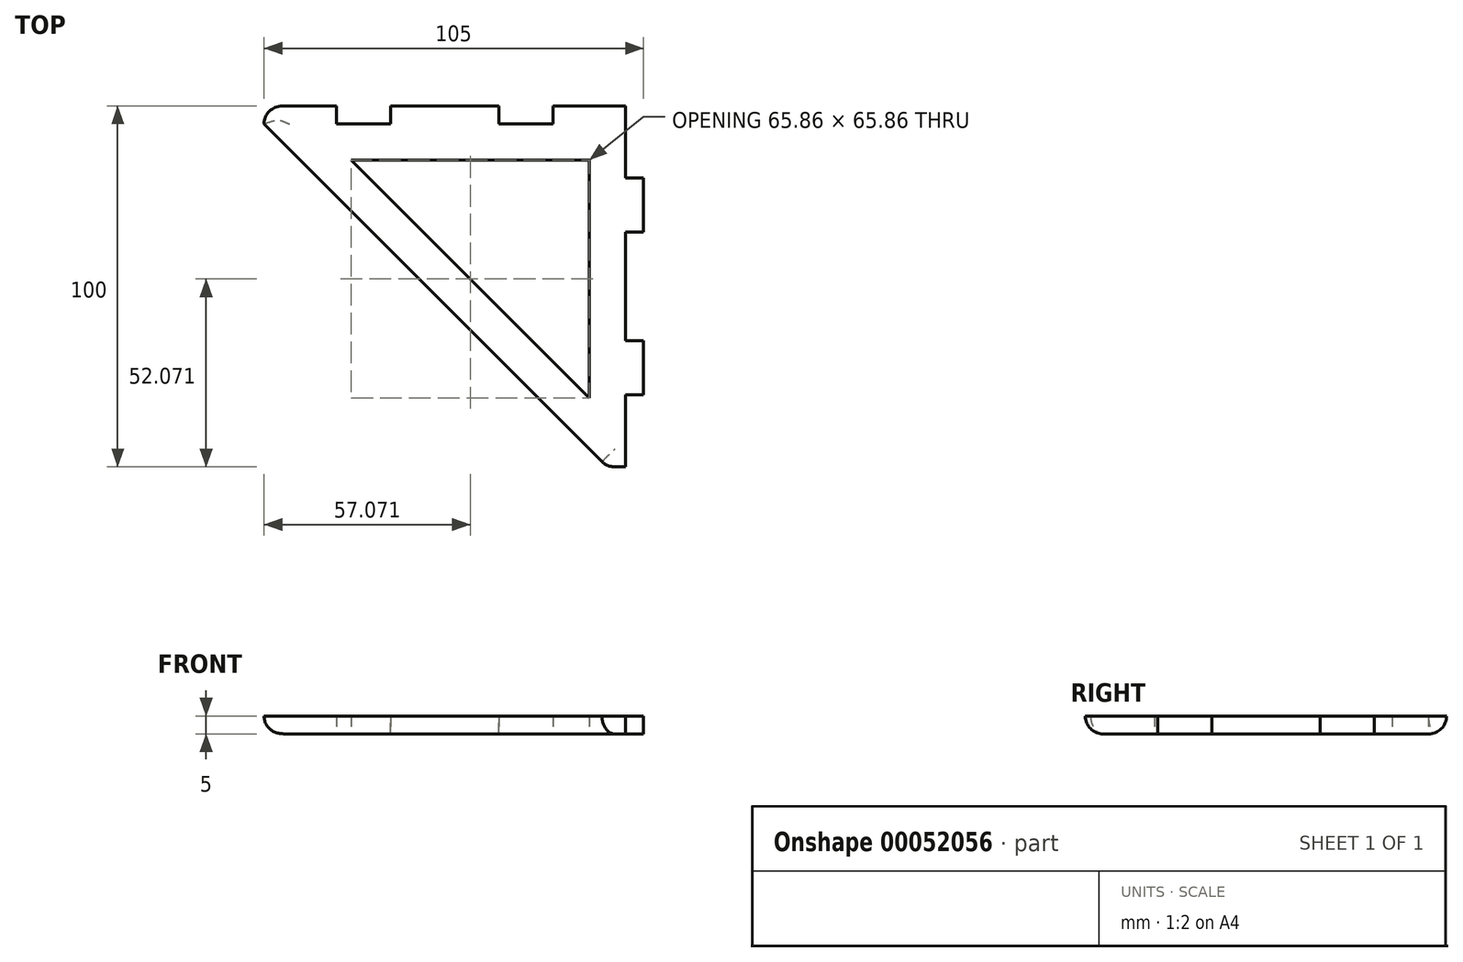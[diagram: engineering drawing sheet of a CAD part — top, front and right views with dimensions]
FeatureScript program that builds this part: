
annotation { "Feature Type Name" : "Feature", "Feature Type Description" : "" }
export const myFeature = defineFeature(function(context is Context, id is Id, definition is map)
    precondition{}
    {
        {
            var Q0;
            Q0=qCreatedBy(makeId("Top.planeOp"),FACE);
            var sketch = newSketch(context, id + "F0", { "sketchPlane" : qUnion([Q0])});
            skLineSegment(sketch, "E0.bottom", {"start": v(-50, 50) * mm, "end": v(-30, 50) * mm});
            skLineSegment(sketch, "E0.right", {"start": v(50, 50) * mm, "end": v(50, 30) * mm});
            skLineSegment(sketch, "E1", {"start": v(-30, 45) * mm, "end": v(-30, 50) * mm});
            skLineSegment(sketch, "E2", {"start": v(-30, 45) * mm, "end": v(-15, 45) * mm});
            skLineSegment(sketch, "E3", {"start": v(-15, 50) * mm, "end": v(-15, 45) * mm});
            skLineSegment(sketch, "E4", {"start": v(30, 45) * mm, "end": v(30, 50) * mm});
            skLineSegment(sketch, "E5", {"start": v(30, 45) * mm, "end": v(15, 45) * mm});
            skLineSegment(sketch, "E6", {"start": v(15, 50) * mm, "end": v(15, 45) * mm});
            skLineSegment(sketch, "E7", {"start": v(55, 30) * mm, "end": v(55, 15) * mm});
            skLineSegment(sketch, "E8", {"start": v(55, -15) * mm, "end": v(55, -30) * mm});
            skLineSegment(sketch, "E9.trimOffspring", {"start": v(-15, 50) * mm, "end": v(15, 50) * mm});
            skLineSegment(sketch, "E10.trimOffspring", {"start": v(30, 50) * mm, "end": v(50, 50) * mm});
            skLineSegment(sketch, "E11.trimOffspring", {"start": v(50, 15) * mm, "end": v(50, -15) * mm});
            skLineSegment(sketch, "E12.trimOffspring", {"start": v(50, -30) * mm, "end": v(50, -50) * mm});
            skLineSegment(sketch, "E13", {"start": v(55, -30) * mm, "end": v(50, -30) * mm});
            skLineSegment(sketch, "E14", {"start": v(50, -15) * mm, "end": v(55, -15) * mm});
            skLineSegment(sketch, "E15", {"start": v(55, 15) * mm, "end": v(50, 15) * mm});
            skLineSegment(sketch, "E16", {"start": v(50, 30) * mm, "end": v(55, 30) * mm});
            skLineSegment(sketch, "E17", {"start": v(-50, 50) * mm, "end": v(-50, 45) * mm});
            skLineSegment(sketch, "E18", {"start": v(50, -50) * mm, "end": v(45, -50) * mm});
            skLineSegment(sketch, "E19", {"start": v(-50, 45) * mm, "end": v(45, -50) * mm});
            skLineSegment(sketch, "E20", {"start": v(22.5, 45) * mm, "end": v(22.5, 35) * mm, "construction": true});
            skLineSegment(sketch, "E21", {"start": v(50, 1.88) * mm, "end": v(40, 1.88) * mm, "construction": true});
            skLineSegment(sketch, "E22", {"start": v(-2.5, -2.5) * mm, "end": v(4.57, 4.57) * mm, "construction": true});
            skLineSegment(sketch, "E23", {"start": v(40, -30.86) * mm, "end": v(40, 35) * mm});
            skLineSegment(sketch, "E24", {"start": v(40, -30.86) * mm, "end": v(-25.86, 35) * mm});
            skLineSegment(sketch, "E25", {"start": v(-25.86, 35) * mm, "end": v(40, 35) * mm});
            skSolve(sketch);
        }
        {
            var Q0;
            Q0=makeQuery(id+"F0.imprint","IMPRINT",FACE,{"disambiguationData":[TD([[makeQuery(id+"F0.imprint","IMPRINT",EDGE,{"derivedFrom":sQuery(id+"F0.wireOp",EDGE,"E0.bottom")}),-1.0]])]});
            extrude(context, id + "F1", {"entities" : qUnion([Q0]), "depth" : 5 * mm});
        }
        {
            var Q0;
            Q0=makeQuery(id+"F1.opExtrude","CAP_EDGE",EDGE,{"disambiguationData":[OSD([sQuery(id+"F0.wireOp",EDGE,"E10.trimOffspring")])],"isStart":true});
            var Q1;
            Q1=makeQuery(id+"F1.opExtrude","CAP_EDGE",EDGE,{"disambiguationData":[OSD([sQuery(id+"F0.wireOp",EDGE,"E9.trimOffspring")])],"isStart":true});
            var Q2;
            Q2=makeQuery(id+"F1.opExtrude","CAP_EDGE",EDGE,{"disambiguationData":[OSD([sQuery(id+"F0.wireOp",EDGE,"E0.bottom")])],"isStart":true});
            var Q3;
            Q3=makeQuery(id+"F1.opExtrude","CAP_EDGE",EDGE,{"disambiguationData":[OSD([sQuery(id+"F0.wireOp",EDGE,"E19")])],"isStart":true});
            fillet(context, id + "F2", {"entities" : qUnion([Q0, Q1, Q2, Q3]), "radius" : 5 * mm, "tangentPropagation" : true, "allowEdgeOverflow" : false});
        }
        {
            var Q0;
            Q0=makeQuery(id+"F2.opFillet","BLEND_EDGE",EDGE,{"blendedFrom":[makeQuery(id+"F1.opExtrude","CAP_EDGE",EDGE,{"disambiguationData":[OSD([sQuery(id+"F0.wireOp",EDGE,"E0.bottom")])],"isStart":true}),makeQuery(id+"F1.opExtrude","SWEPT_FACE",FACE,{"disambiguationData":[OSD([sQuery(id+"F0.wireOp",EDGE,"E17")])]})],"blendedInto":[makeQuery(id+"F1.opExtrude","SWEPT_FACE",FACE,{"disambiguationData":[OSD([sQuery(id+"F0.wireOp",EDGE,"E17")])]})]});
            fillet(context, id + "F3", {"entities" : qUnion([Q0]), "radius" : 5 * mm, "tangentPropagation" : true, "allowEdgeOverflow" : false});
        }
        {
            var Q0;
            Q0=makeQuery(id+"F2.opFillet","BLEND_EDGE",EDGE,{"blendedFrom":[makeQuery(id+"F1.opExtrude","CAP_EDGE",EDGE,{"disambiguationData":[OSD([sQuery(id+"F0.wireOp",EDGE,"E19")])],"isStart":true}),makeQuery(id+"F1.opExtrude","SWEPT_FACE",FACE,{"disambiguationData":[OSD([sQuery(id+"F0.wireOp",EDGE,"E18")])]})],"blendedInto":[makeQuery(id+"F1.opExtrude","SWEPT_FACE",FACE,{"disambiguationData":[OSD([sQuery(id+"F0.wireOp",EDGE,"E18")])]})]});
            fillet(context, id + "F4", {"entities" : qUnion([Q0]), "radius" : 5 * mm, "tangentPropagation" : true, "allowEdgeOverflow" : false});
        }
    });
